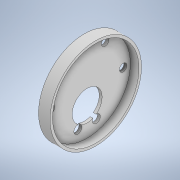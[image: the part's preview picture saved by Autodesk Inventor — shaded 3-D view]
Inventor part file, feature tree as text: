
AUTODESK INVENTOR PART (.ipt)
format: ipt  version: 2020 (Build 240168000, 168)  size: 224,768 bytes
history: native  units: in
note: dims shown in document units (in); Inventor stores cm internally (conversion verified against a paired STEP export)
features: sketch x9, extrude x8, fillet x2, hole x1
ambient origin geometry x8: Origin, YZ Plane, XZ Plane, XY Plane, X Axis, Y Axis, Z Axis, Center Point
bodies: Solid1 (feature_tree)
feature tree (20):
  extrude  "Extrusion1"  Depth=3.0in
  extrude  "Extrusion2"  Depth=0.5in
  extrude  "Extrusion3"  Depth=2.0in
  fillet  "Fillet1"  Radius=1.7in
  sketch  "Sketch6"  dims[d10=1.5in d11=0.6in d12=0.0in]
  fillet  "Fillet2"  Radius=1.0in
  hole  "Hole1"  [1 undecoded]
  extrude  "Extrusion5"  Depth=0.25in
  extrude  "Extrusion7"  Depth=1.0in
  extrude  "Extrusion8"  Depth=0.15in
  extrude  "Extrusion9"  Depth=0.6in TaperAngle=0.0deg
  extrude  "Extrusion10"  TaperAngle=120.0deg  [1 undecoded]
  sketch  "Sketch1"  dims[d0=0.8in d1=3.0in]
  sketch  "Sketch2"  dims[d2=0.3in d3=0.0in d4=0.5in]
  sketch  "Sketch3"  dims[d5=0.8in d6=2.0in d7=1.7in d8=0.0in d9=1.0in]
  sketch  "Sketch7"  dims[d19=1.0in d20=0.25in]
  sketch  "Sketch9"  dims[d21=0.25in d22=1.0in]
  sketch  "Sketch10"  dims[d23=0.2in d24=0.75in d25=0.4in d26=0.15in d27=0.5635in d28=1.0in d29=0.8108in d30=0.4in]
  sketch  "Sketch11"  dims[d31=0.4in d32=0.6in d33=0.0in]
  sketch  "Sketch12"  dims[d47=0.26in d48=120.0deg d49=60.0deg d50=0.06in d51=0.06in d52=60.0deg d53=0.14in d54=0.14in d55=0.06in d56=0.065in d57=0.06in d58=0.065in d59=0.06in d60=0.065in d61=0.06in d62=0.065in d63=1.0in d64=0.0in d65=2.0in d66=0.0in d67=0.15in d68=0.0in d69=0.6in d70=0.0in]
note: 2 required parameter values undecoded (feature->parameter linkage not recoverable at this tier; creation-order binding heuristic only, values carry confidence <= 0.55)
